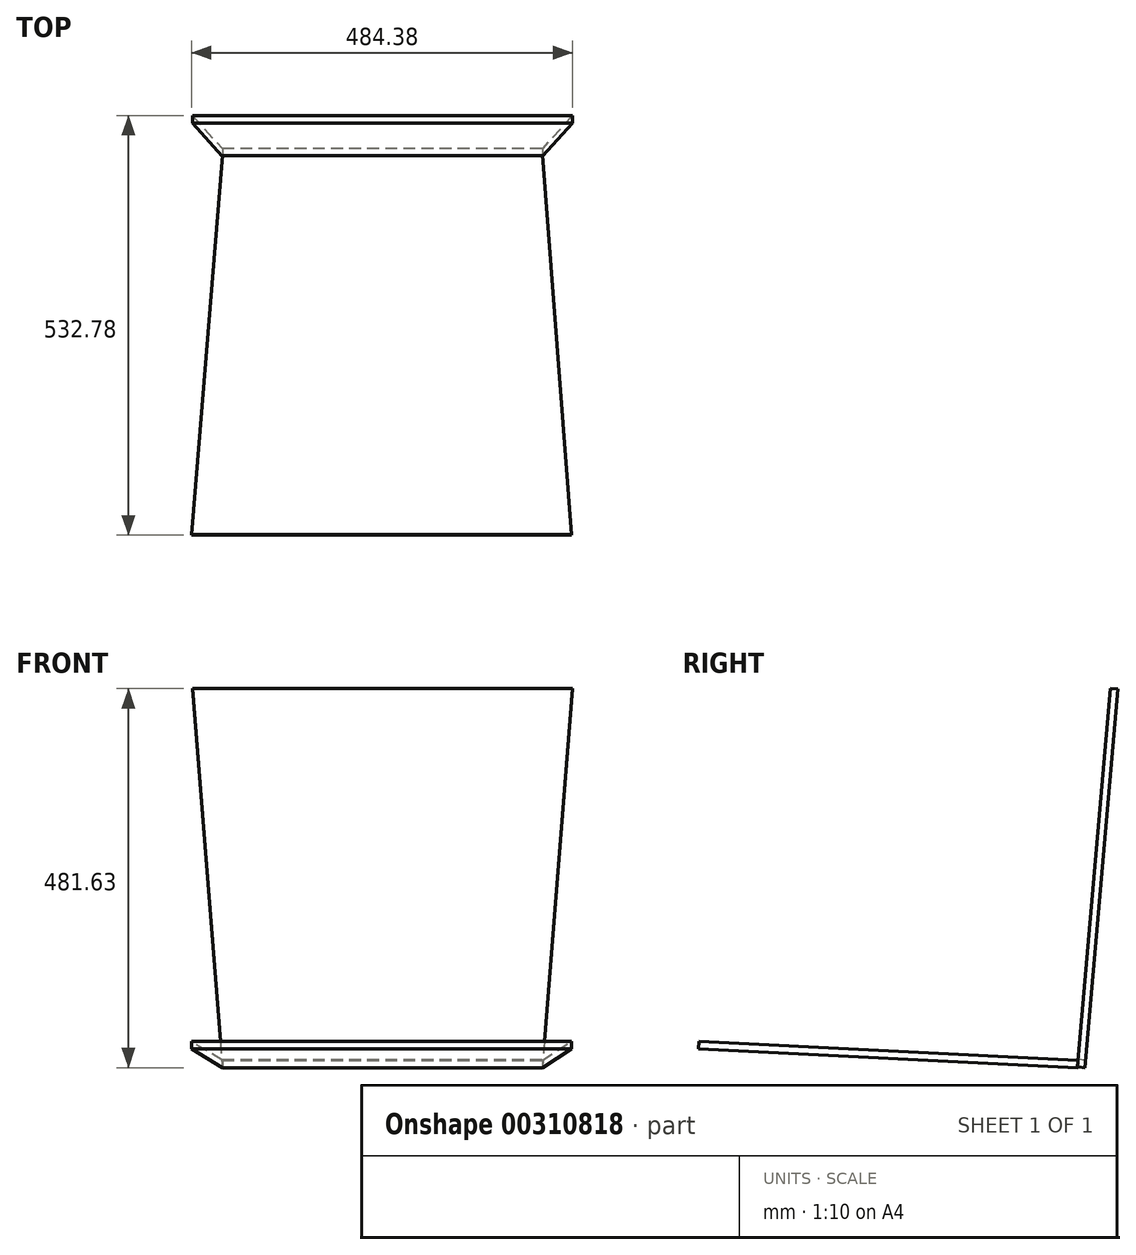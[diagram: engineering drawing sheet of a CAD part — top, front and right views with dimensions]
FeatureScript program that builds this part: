
annotation { "Feature Type Name" : "Feature", "Feature Type Description" : "" }
export const myFeature = defineFeature(function(context is Context, id is Id, definition is map)
    precondition{}
    {
        {
            var Q0;
            Q0=qCreatedBy(makeId("Top.planeOp"),FACE);
            var sketch = newSketch(context, id + "F0", { "sketchPlane" : qUnion([Q0])});
            skLineSegment(sketch, "E0", {"start": v(-47.64, 43.61) * mm, "end": v(358.76, 43.61) * mm});
            skLineSegment(sketch, "E1", {"start": v(-87.04, -438.99) * mm, "end": v(395.56, -438.99) * mm});
            skLineSegment(sketch, "E2", {"start": v(-47.64, 43.61) * mm, "end": v(-87.04, -438.99) * mm});
            skLineSegment(sketch, "E3", {"start": v(358.76, 43.61) * mm, "end": v(395.56, -438.99) * mm});
            skSolve(sketch);
        }
        {
            var Q0;
            Q0=makeQuery(id+"F0.imprint","IMPRINT",FACE,{"disambiguationData":[TD([[makeQuery(id+"F0.imprint","IMPRINT",EDGE,{"derivedFrom":sQuery(id+"F0.wireOp",EDGE,"E0")}),-1.0]])]});
            extrude(context, id + "F1", {"entities" : qUnion([Q0]), "depth" : 9.52 * mm});
        }
        {
            var Q0;
            Q0=makeQuery(id+"F1.opExtrude","SWEPT_FACE",FACE,{"disambiguationData":[OSD([sQuery(id+"F0.wireOp",EDGE,"E0")])]});
            var sketch = newSketch(context, id + "F2", { "sketchPlane" : qUnion([Q0])});
            skLineSegment(sketch, "E4", {"start": v(-358.76, 0) * mm, "end": v(47.64, 0) * mm});
            skLineSegment(sketch, "E5", {"start": v(-397.34, 482.6) * mm, "end": v(85.26, 482.6) * mm});
            skLineSegment(sketch, "E6", {"start": v(-397.34, 482.6) * mm, "end": v(-358.76, 0) * mm});
            skLineSegment(sketch, "E7", {"start": v(85.26, 482.6) * mm, "end": v(47.64, 0) * mm});
            skSolve(sketch);
        }
        {
            var Q0;
            Q0=makeQuery(id+"F2.imprint","IMPRINT",FACE,{"disambiguationData":[TD([[makeQuery(id+"F2.imprint","IMPRINT",EDGE,{"derivedFrom":sQuery(id+"F2.wireOp",EDGE,"E5")}),-1.0]])]});
            extrude(context, id + "F3", {"entities" : qUnion([Q0]), "depth" : 9.52 * mm});
        }
        {
            var Q0;
            Q0=makeQuery(id+"F3.opExtrude","SWEPT_BODY",BODY,{"disambiguationData":[OSD([sQuery(id+"F0.wireOp",EDGE,"E0"),sQuery(id+"F0.wireOp",EDGE,"E2"),sQuery(id+"F0.wireOp",EDGE,"E3"),sQuery(id+"F2.wireOp",EDGE,"E5"),sQuery(id+"F2.wireOp",EDGE,"E6"),sQuery(id+"F2.wireOp",EDGE,"E7")])]});
            var Q1;
            Q1=makeQuery(id+"F3.opExtrude","CAP_EDGE",EDGE,{"disambiguationData":[OSD([sQuery(id+"F0.wireOp",EDGE,"E0")])],"isStart":false});
            transform(context, id + "F4", {"entities" : qUnion([Q0]), "transformType" : TransformType.ROTATION, "transformAxis" : qUnion([Q1]), "angle" : 5 * degree, "oppositeDirection" : true, "makeCopy" : false});
        }
        {
            var Q0;
            Q0=makeQuery(id+"F1.opExtrude","SWEPT_BODY",BODY,{"disambiguationData":[OSD([sQuery(id+"F0.wireOp",EDGE,"E0"),sQuery(id+"F0.wireOp",EDGE,"E1"),sQuery(id+"F0.wireOp",EDGE,"E2"),sQuery(id+"F0.wireOp",EDGE,"E3")])]});
            var Q1;
            Q1=makeQuery(id+"F1.opExtrude","CAP_EDGE",EDGE,{"disambiguationData":[OSD([sQuery(id+"F0.wireOp",EDGE,"E0")])],"isStart":true});
            transform(context, id + "F5", {"entities" : qUnion([Q0]), "transformType" : TransformType.ROTATION, "transformAxis" : qUnion([Q1]), "angle" : 2.8 * degree, "oppositeDirection" : true, "makeCopy" : false});
        }
        {
            var Q0;
            Q0=makeQuery(id+"F1.opExtrude","SWEPT_BODY",BODY,{"disambiguationData":[OSD([sQuery(id+"F0.wireOp",EDGE,"E0"),sQuery(id+"F0.wireOp",EDGE,"E1"),sQuery(id+"F0.wireOp",EDGE,"E2"),sQuery(id+"F0.wireOp",EDGE,"E3")])]});
            transform(context, id + "F6", {"entities" : qUnion([Q0]), "transformType" : TransformType.TRANSLATION_3D, "dx" : 0 * mm, "dy" : 0 * mm, "dz" : -508 * mm, "makeCopy" : true});
        }
        {
            var Q0;
            Q0=makeQuery(id+"F6.opPattern","COPY",BODY,{"derivedFrom":makeQuery(id+"F1.opExtrude","SWEPT_BODY",BODY,{"disambiguationData":[OSD([sQuery(id+"F0.wireOp",EDGE,"E0"),sQuery(id+"F0.wireOp",EDGE,"E1"),sQuery(id+"F0.wireOp",EDGE,"E2"),sQuery(id+"F0.wireOp",EDGE,"E3")])]}),"instanceName":"1"});
            deleteBodies(context, id + "F7", {"entities" : qUnion([Q0])});
        }
    });
